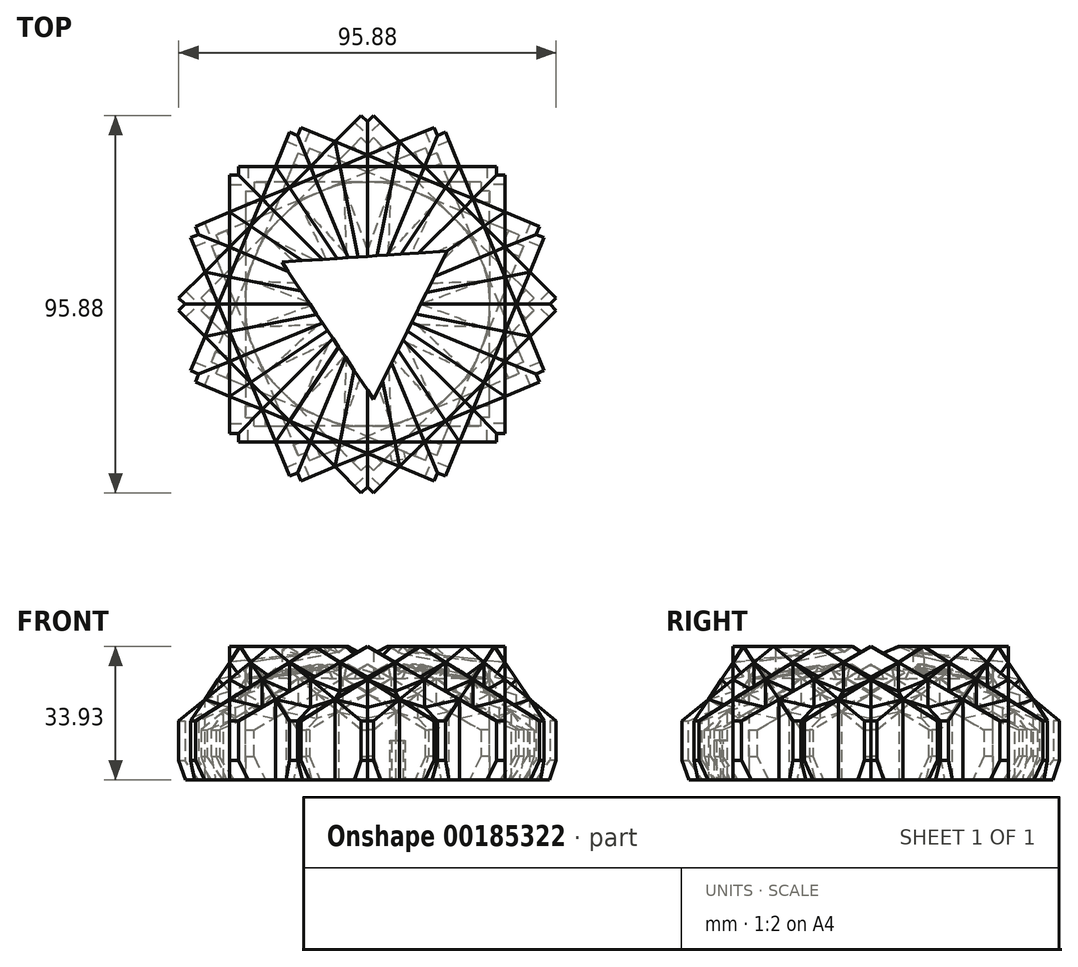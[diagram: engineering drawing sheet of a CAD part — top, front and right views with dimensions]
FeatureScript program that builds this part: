
annotation { "Feature Type Name" : "Feature", "Feature Type Description" : "" }
export const myFeature = defineFeature(function(context is Context, id is Id, definition is map)
    precondition{}
    {
        {
            var Q0;
            Q0=qCreatedBy(makeId("Front.planeOp"),FACE);
            var sketch = newSketch(context, id + "F0", { "sketchPlane" : qUnion([Q0])});
            skLineSegment(sketch, "E0", {"start": v(4.08, -77.3) * mm, "end": v(4.08, 73.55) * mm, "construction": true});
            skCircle(sketch, "E1.cCircle", {"center": v(4.08, -2.77) * mm, "radius": 37.87 * mm, "construction": true});
            skLineSegment(sketch, "E1.0", {"start": v(4.08, 35.1) * mm, "end": v(36.87, -21.7) * mm});
            skLineSegment(sketch, "E1.1", {"start": v(36.87, -21.7) * mm, "end": v(-28.71, -21.7) * mm});
            skLineSegment(sketch, "E1.2", {"start": v(-28.71, -21.7) * mm, "end": v(4.08, 35.1) * mm});
            skLineSegment(sketch, "E2.0", {"start": v(4.08, 35.1) * mm, "end": v(36.87, 16.17) * mm});
            skLineSegment(sketch, "E2.1", {"start": v(36.87, 16.17) * mm, "end": v(36.87, -21.7) * mm});
            skLineSegment(sketch, "E2.2", {"start": v(36.87, -21.7) * mm, "end": v(4.08, -40.63) * mm});
            skLineSegment(sketch, "E2.3", {"start": v(4.08, -40.63) * mm, "end": v(-28.71, -21.7) * mm});
            skLineSegment(sketch, "E2.4", {"start": v(-28.71, -21.7) * mm, "end": v(-28.71, 16.17) * mm});
            skLineSegment(sketch, "E2.5", {"start": v(-28.71, 16.17) * mm, "end": v(4.08, 35.1) * mm});
            skLineSegment(sketch, "E3", {"start": v(4.08, -15.7) * mm, "end": v(4.08, -21.7) * mm, "construction": true});
            skLineSegment(sketch, "E4", {"start": v(-28.71, -21.7) * mm, "end": v(-21.71, -21.7) * mm, "construction": true});
            skArc(sketch, "E5", {"start": v(4.08, -15.7) * mm, "mid": v(-9.22, -16.96) * mm, "end": v(-21.71, -21.7) * mm});
            skArc(sketch, "E6.MirrorCS", {"start": v(4.08, -15.7) * mm, "mid": v(17.38, -16.96) * mm, "end": v(29.87, -21.7) * mm});
            skArc(sketch, "E7", {"start": v(-12.32, 25.63) * mm, "mid": v(4.08, 3.7) * mm, "end": v(20.48, 25.63) * mm});
            skLineSegment(sketch, "E8", {"start": v(-12.32, 25.63) * mm, "end": v(-20.53, 16.17) * mm});
            skLineSegment(sketch, "E9", {"start": v(-20.53, 16.17) * mm, "end": v(-28.71, 16.17) * mm});
            skLineSegment(sketch, "E10.MirrorCS", {"start": v(20.48, 25.63) * mm, "end": v(28.7, 16.17) * mm});
            skLineSegment(sketch, "E11.MirrorCS", {"start": v(28.7, 16.17) * mm, "end": v(36.87, 16.17) * mm});
            skLineSegment(sketch, "E12", {"start": v(-28.71, 16.17) * mm, "end": v(-28.71, 6.17) * mm, "construction": true});
            skLineSegment(sketch, "E13", {"start": v(-28.71, 6.17) * mm, "end": v(-28.71, -3.83) * mm, "construction": true});
            skArc(sketch, "E14", {"start": v(-28.71, -3.83) * mm, "mid": v(-26.27, 1.17) * mm, "end": v(-28.71, 6.17) * mm});
            skArc(sketch, "E15.MirrorCS", {"start": v(36.87, -3.83) * mm, "mid": v(34.42, 1.17) * mm, "end": v(36.87, 6.17) * mm});
            skLineSegment(sketch, "E16", {"start": v(-28.71, 1.17) * mm, "end": v(-26.27, 1.17) * mm, "construction": true});
            skLineSegment(sketch, "E17", {"start": v(-28.71, 6.17) * mm, "end": v(-26.27, 1.17) * mm});
            skLineSegment(sketch, "E18", {"start": v(-26.27, 1.17) * mm, "end": v(-28.71, -3.83) * mm});
            skLineSegment(sketch, "E19.MirrorCS", {"start": v(36.87, 6.17) * mm, "end": v(34.42, 1.17) * mm});
            skLineSegment(sketch, "E20.MirrorCS", {"start": v(34.42, 1.17) * mm, "end": v(36.87, -3.83) * mm});
            skLineSegment(sketch, "E21", {"start": v(-28.71, 1.17) * mm, "end": v(36.87, 1.17) * mm});
            skSolve(sketch);
        }
        {
            var Q0;
            {var subQ0=sQuery(id+"F0.wireOp",EDGE,"E8");Q0=makeQuery(id+"F0.imprint","IMPRINT",FACE,{"disambiguationData":[TD([[makeQuery(id+"F0.imprint","IMPRINT",EDGE,{"derivedFrom":subQ0}),1.0]])]});}
            var Q1;
            {var subQ0=sQuery(id+"F0.wireOp",EDGE,"E7");var subQ1=sQuery(id+"F0.wireOp",EDGE,"E1.0");var subQ2=makeQuery(id+"F0.imprint","INTERSECT",VERTEX,{"derivedFrom":[subQ1,subQ0]});Q1=makeQuery(id+"F0.imprint","IMPRINT",FACE,{"disambiguationData":[TD([[makeQuery(id+"F0.imprint","IMPRINT",EDGE,{"disambiguationData":[TD([[subQ2,-1.0]])],"derivedFrom":subQ1}),-1.0]])]});}
            var Q2;
            {var subQ0=sQuery(id+"F0.wireOp",EDGE,"E10.MirrorCS");Q2=makeQuery(id+"F0.imprint","IMPRINT",FACE,{"disambiguationData":[TD([[makeQuery(id+"F0.imprint","IMPRINT",EDGE,{"derivedFrom":subQ0}),-1.0]])]});}
            var Q3;
            {var subQ2=sQuery(id+"F0.wireOp",EDGE,"E10.MirrorCS");Q3=makeQuery(id+"F0.imprint","IMPRINT",FACE,{"disambiguationData":[TD([[makeQuery(id+"F0.imprint","IMPRINT",EDGE,{"derivedFrom":subQ2}),1.0]])]});}
            var Q4;
            {var subQ1=sQuery(id+"F0.wireOp",EDGE,"E1.0");var subQ3=sQuery(id+"F0.wireOp",EDGE,"E7");var subQ4=makeQuery(id+"F0.imprint","INTERSECT",VERTEX,{"derivedFrom":[subQ1,subQ3]});Q4=makeQuery(id+"F0.imprint","IMPRINT",FACE,{"disambiguationData":[TD([[makeQuery(id+"F0.imprint","IMPRINT",EDGE,{"disambiguationData":[TD([[subQ4,-1.0]])],"derivedFrom":subQ3}),1.0]])]});}
            var Q5;
            {var subQ1=sQuery(id+"F0.wireOp",EDGE,"E1.2");var subQ3=sQuery(id+"F0.wireOp",EDGE,"E7");var subQ4=makeQuery(id+"F0.imprint","INTERSECT",VERTEX,{"derivedFrom":[subQ1,subQ3]});Q5=makeQuery(id+"F0.imprint","IMPRINT",FACE,{"disambiguationData":[TD([[makeQuery(id+"F0.imprint","IMPRINT",EDGE,{"disambiguationData":[TD([[subQ4,1.0]])],"derivedFrom":subQ3}),1.0]])]});}
            var Q6;
            {var subQ0=sQuery(id+"F0.wireOp",EDGE,"E17");Q6=makeQuery(id+"F0.imprint","IMPRINT",FACE,{"disambiguationData":[TD([[makeQuery(id+"F0.imprint","IMPRINT",EDGE,{"derivedFrom":subQ0}),1.0]])]});}
            var Q7;
            {var subQ0=sQuery(id+"F0.wireOp",EDGE,"E19.MirrorCS");Q7=makeQuery(id+"F0.imprint","IMPRINT",FACE,{"disambiguationData":[TD([[makeQuery(id+"F0.imprint","IMPRINT",EDGE,{"derivedFrom":subQ0}),-1.0]])]});}
            var Q8;
            {var subQ1=sQuery(id+"F0.wireOp",EDGE,"E1.0");var subQ3=sQuery(id+"F0.wireOp",EDGE,"E7");var subQ4=makeQuery(id+"F0.imprint","INTERSECT",VERTEX,{"derivedFrom":[subQ1,subQ3]});Q8=makeQuery(id+"F0.imprint","IMPRINT",FACE,{"disambiguationData":[TD([[makeQuery(id+"F0.imprint","IMPRINT",EDGE,{"disambiguationData":[TD([[subQ4,1.0]])],"derivedFrom":subQ3}),1.0]])]});}
            var Q9;
            {var subQ2=sQuery(id+"F0.wireOp",EDGE,"E8");Q9=makeQuery(id+"F0.imprint","IMPRINT",FACE,{"disambiguationData":[TD([[makeQuery(id+"F0.imprint","IMPRINT",EDGE,{"derivedFrom":subQ2}),-1.0]])]});}
            var Q10;
            {var subQ1=sQuery(id+"F0.wireOp",EDGE,"E1.0");var subQ3=sQuery(id+"F0.wireOp",EDGE,"6VoTTzTf-1nzT-aMky-r3Jn-bNhaZYPHa5TC");var subQ4=makeQuery(id+"F0.imprint","INTERSECT",VERTEX,{"derivedFrom":[subQ1,subQ3]});Q10=makeQuery(id+"F0.imprint","IMPRINT",FACE,{"disambiguationData":[TD([[makeQuery(id+"F0.imprint","IMPRINT",EDGE,{"disambiguationData":[TD([[subQ4,-1.0]])],"derivedFrom":subQ3}),-1.0]])]});}
            var Q11;
            Q11=sQuery(id+"F0.wireOp",EDGE,"E1.0");
            var Q12;
            Q12=sQuery(id+"F0.wireOp",EDGE,"E1.1");
            var Q13;
            Q13=sQuery(id+"F0.wireOp",EDGE,"E1.2");
            var Q14;
            Q14=sQuery(id+"F0.wireOp",EDGE,"E2.0");
            var Q15;
            Q15=sQuery(id+"F0.wireOp",EDGE,"E2.1");
            var Q16;
            Q16=sQuery(id+"F0.wireOp",EDGE,"E2.2");
            var Q17;
            Q17=sQuery(id+"F0.wireOp",EDGE,"E2.3");
            var Q18;
            Q18=sQuery(id+"F0.wireOp",EDGE,"E2.4");
            var Q19;
            Q19=sQuery(id+"F0.wireOp",EDGE,"E2.5");
            var Q20;
            Q20=sQuery(id+"F0.wireOp",EDGE,"E5");
            var Q21;
            Q21=sQuery(id+"F0.wireOp",EDGE,"E6.MirrorCS");
            var Q22;
            Q22=sQuery(id+"F0.wireOp",EDGE,"E7");
            var Q23;
            Q23=sQuery(id+"F0.wireOp",EDGE,"E8");
            var Q24;
            Q24=sQuery(id+"F0.wireOp",EDGE,"E9");
            var Q25;
            Q25=sQuery(id+"F0.wireOp",EDGE,"E10.MirrorCS");
            var Q26;
            Q26=sQuery(id+"F0.wireOp",EDGE,"E11.MirrorCS");
            var Q27;
            Q27=sQuery(id+"F0.wireOp",EDGE,"E14");
            var Q28;
            Q28=sQuery(id+"F0.wireOp",EDGE,"E15.MirrorCS");
            var Q29;
            Q29=sQuery(id+"F0.wireOp",EDGE,"E17");
            var Q30;
            Q30=sQuery(id+"F0.wireOp",EDGE,"E18");
            var Q31;
            Q31=sQuery(id+"F0.wireOp",EDGE,"E19.MirrorCS");
            var Q32;
            Q32=sQuery(id+"F0.wireOp",EDGE,"E20.MirrorCS");
            var Q33;
            Q33=sQuery(id+"F0.wireOp",EDGE,"E21");
            extrude(context, id + "F1", {"entities" : qUnion([Q0, Q1, Q2, Q3, Q4, Q5, Q6, Q7, Q8, Q9, Q10]), "surfaceEntities" : qUnion([Q11, Q12, Q13, Q14, Q15, Q16, Q17, Q18, Q19, Q20, Q21, Q22, Q23, Q24, Q25, Q26, Q27, Q28, Q29, Q30, Q31, Q32, Q33]), "offsetDistance" : 25 * mm, "depth" : 35 * mm});
        }
        {
            var Q0;
            Q0=makeQuery(id+"F1.opExtrude","SWEPT_BODY",BODY,{"disambiguationData":[OSD([sQuery(id+"F0.wireOp",EDGE,"E2.0"),sQuery(id+"F0.wireOp",EDGE,"E2.1"),sQuery(id+"F0.wireOp",EDGE,"E2.4"),sQuery(id+"F0.wireOp",EDGE,"E2.5"),sQuery(id+"F0.wireOp",EDGE,"E17"),sQuery(id+"F0.wireOp",EDGE,"E19.MirrorCS"),sQuery(id+"F0.wireOp",EDGE,"E21")])]});
            var Q1;
            Q1=sQuery(id+"F0.wireOp",EDGE,"E0");
            circularPattern(context, id + "F2", {"operationType" : NewBodyOperationType.ADD, "entities" : qUnion([Q0]), "axis" : qUnion([Q1]), "angle" : 360 * degree, "instanceCount" : 16, "equalSpace" : true, "isCentered" : true});
        }
        {
            var Q0;
            {var subQ0=makeQuery(id+"F1.opExtrude","SWEPT_FACE",FACE,{"disambiguationData":[OSD([sQuery(id+"F0.wireOp",EDGE,"E21")])]});Q0=makeQuery(id+"F2.boolean.opBoolean","MERGE",FACE,{"derivedFrom":[subQ0,makeQuery(id+"F2.opPattern","COPY",FACE,{"derivedFrom":subQ0,"instanceName":"-15"}),makeQuery(id+"F2.opPattern","COPY",FACE,{"derivedFrom":subQ0,"instanceName":"-14"}),makeQuery(id+"F2.opPattern","COPY",FACE,{"derivedFrom":subQ0,"instanceName":"-13"}),makeQuery(id+"F2.opPattern","COPY",FACE,{"derivedFrom":subQ0,"instanceName":"-12"}),makeQuery(id+"F2.opPattern","COPY",FACE,{"derivedFrom":subQ0,"instanceName":"-11"}),makeQuery(id+"F2.opPattern","COPY",FACE,{"derivedFrom":subQ0,"instanceName":"-10"}),makeQuery(id+"F2.opPattern","COPY",FACE,{"derivedFrom":subQ0,"instanceName":"-9"}),makeQuery(id+"F2.opPattern","COPY",FACE,{"derivedFrom":subQ0,"instanceName":"-8"}),makeQuery(id+"F2.opPattern","COPY",FACE,{"derivedFrom":subQ0,"instanceName":"-7"}),makeQuery(id+"F2.opPattern","COPY",FACE,{"derivedFrom":subQ0,"instanceName":"-6"}),makeQuery(id+"F2.opPattern","COPY",FACE,{"derivedFrom":subQ0,"instanceName":"-5"}),makeQuery(id+"F2.opPattern","COPY",FACE,{"derivedFrom":subQ0,"instanceName":"-4"}),makeQuery(id+"F2.opPattern","COPY",FACE,{"derivedFrom":subQ0,"instanceName":"-3"}),makeQuery(id+"F2.opPattern","COPY",FACE,{"derivedFrom":subQ0,"instanceName":"-2"}),makeQuery(id+"F2.opPattern","COPY",FACE,{"derivedFrom":subQ0,"instanceName":"-1"}),makeQuery(id+"F2.opPattern","COPY",FACE,{"derivedFrom":subQ0,"instanceName":"1"}),makeQuery(id+"F2.opPattern","COPY",FACE,{"derivedFrom":subQ0,"instanceName":"2"}),makeQuery(id+"F2.opPattern","COPY",FACE,{"derivedFrom":subQ0,"instanceName":"3"}),makeQuery(id+"F2.opPattern","COPY",FACE,{"derivedFrom":subQ0,"instanceName":"4"}),makeQuery(id+"F2.opPattern","COPY",FACE,{"derivedFrom":subQ0,"instanceName":"5"}),makeQuery(id+"F2.opPattern","COPY",FACE,{"derivedFrom":subQ0,"instanceName":"6"}),makeQuery(id+"F2.opPattern","COPY",FACE,{"derivedFrom":subQ0,"instanceName":"7"}),makeQuery(id+"F2.opPattern","COPY",FACE,{"derivedFrom":subQ0,"instanceName":"8"}),makeQuery(id+"F2.opPattern","COPY",FACE,{"derivedFrom":subQ0,"instanceName":"9"}),makeQuery(id+"F2.opPattern","COPY",FACE,{"derivedFrom":subQ0,"instanceName":"10"}),makeQuery(id+"F2.opPattern","COPY",FACE,{"derivedFrom":subQ0,"instanceName":"11"}),makeQuery(id+"F2.opPattern","COPY",FACE,{"derivedFrom":subQ0,"instanceName":"12"}),makeQuery(id+"F2.opPattern","COPY",FACE,{"derivedFrom":subQ0,"instanceName":"13"}),makeQuery(id+"F2.opPattern","COPY",FACE,{"derivedFrom":subQ0,"instanceName":"14"}),makeQuery(id+"F2.opPattern","COPY",FACE,{"derivedFrom":subQ0,"instanceName":"15"})]});}
            shell(context, id + "F3", {"entities" : qUnion([Q0]), "thickness" : 4 * mm});
        }
        {
            var Q0;
            {var subQ0=makeQuery(id+"F1.opExtrude","SWEPT_FACE",FACE,{"disambiguationData":[OSD([sQuery(id+"F0.wireOp",EDGE,"E21")])]});Q0=makeQuery(id+"F2.boolean.opBoolean","MERGE",FACE,{"derivedFrom":[subQ0,makeQuery(id+"F2.opPattern","COPY",FACE,{"derivedFrom":subQ0,"instanceName":"-15"}),makeQuery(id+"F2.opPattern","COPY",FACE,{"derivedFrom":subQ0,"instanceName":"-14"}),makeQuery(id+"F2.opPattern","COPY",FACE,{"derivedFrom":subQ0,"instanceName":"-13"}),makeQuery(id+"F2.opPattern","COPY",FACE,{"derivedFrom":subQ0,"instanceName":"-12"}),makeQuery(id+"F2.opPattern","COPY",FACE,{"derivedFrom":subQ0,"instanceName":"-11"}),makeQuery(id+"F2.opPattern","COPY",FACE,{"derivedFrom":subQ0,"instanceName":"-10"}),makeQuery(id+"F2.opPattern","COPY",FACE,{"derivedFrom":subQ0,"instanceName":"-9"}),makeQuery(id+"F2.opPattern","COPY",FACE,{"derivedFrom":subQ0,"instanceName":"-8"}),makeQuery(id+"F2.opPattern","COPY",FACE,{"derivedFrom":subQ0,"instanceName":"-7"}),makeQuery(id+"F2.opPattern","COPY",FACE,{"derivedFrom":subQ0,"instanceName":"-6"}),makeQuery(id+"F2.opPattern","COPY",FACE,{"derivedFrom":subQ0,"instanceName":"-5"}),makeQuery(id+"F2.opPattern","COPY",FACE,{"derivedFrom":subQ0,"instanceName":"-4"}),makeQuery(id+"F2.opPattern","COPY",FACE,{"derivedFrom":subQ0,"instanceName":"-3"}),makeQuery(id+"F2.opPattern","COPY",FACE,{"derivedFrom":subQ0,"instanceName":"-2"}),makeQuery(id+"F2.opPattern","COPY",FACE,{"derivedFrom":subQ0,"instanceName":"-1"}),makeQuery(id+"F2.opPattern","COPY",FACE,{"derivedFrom":subQ0,"instanceName":"1"}),makeQuery(id+"F2.opPattern","COPY",FACE,{"derivedFrom":subQ0,"instanceName":"2"}),makeQuery(id+"F2.opPattern","COPY",FACE,{"derivedFrom":subQ0,"instanceName":"3"}),makeQuery(id+"F2.opPattern","COPY",FACE,{"derivedFrom":subQ0,"instanceName":"4"}),makeQuery(id+"F2.opPattern","COPY",FACE,{"derivedFrom":subQ0,"instanceName":"5"}),makeQuery(id+"F2.opPattern","COPY",FACE,{"derivedFrom":subQ0,"instanceName":"6"}),makeQuery(id+"F2.opPattern","COPY",FACE,{"derivedFrom":subQ0,"instanceName":"7"}),makeQuery(id+"F2.opPattern","COPY",FACE,{"derivedFrom":subQ0,"instanceName":"8"}),makeQuery(id+"F2.opPattern","COPY",FACE,{"derivedFrom":subQ0,"instanceName":"9"}),makeQuery(id+"F2.opPattern","COPY",FACE,{"derivedFrom":subQ0,"instanceName":"10"}),makeQuery(id+"F2.opPattern","COPY",FACE,{"derivedFrom":subQ0,"instanceName":"11"}),makeQuery(id+"F2.opPattern","COPY",FACE,{"derivedFrom":subQ0,"instanceName":"12"}),makeQuery(id+"F2.opPattern","COPY",FACE,{"derivedFrom":subQ0,"instanceName":"13"}),makeQuery(id+"F2.opPattern","COPY",FACE,{"derivedFrom":subQ0,"instanceName":"14"}),makeQuery(id+"F2.opPattern","COPY",FACE,{"derivedFrom":subQ0,"instanceName":"15"})]});}
            var sketch = newSketch(context, id + "F4", { "sketchPlane" : qUnion([Q0])});
            skLineSegment(sketch, "E22.bottom", {"start": v(9.25, 34.95) * mm, "end": v(12.68, 34.26) * mm});
            skLineSegment(sketch, "E22.top", {"start": v(10.22, 39.85) * mm, "end": v(13.65, 39.17) * mm});
            skLineSegment(sketch, "E22.left", {"start": v(9.25, 34.95) * mm, "end": v(10.22, 39.85) * mm});
            skLineSegment(sketch, "E22.right", {"start": v(12.68, 34.26) * mm, "end": v(13.65, 39.17) * mm});
            skPoint(sketch, "E22.middle", {"position": v(11.45, 37.06) * mm});
            skLineSegment(sketch, "E23", {"start": v(11.35, 36.57) * mm, "end": v(11.94, 39.5) * mm, "construction": true});
            skLineSegment(sketch, "E24", {"start": v(11.45, 37.06) * mm, "end": v(13.17, 36.72) * mm, "construction": true});
            skLineSegment(sketch, "E25", {"start": v(11.45, 37.06) * mm, "end": v(9.73, 37.4) * mm, "construction": true});
            skLineSegment(sketch, "E26", {"start": v(12.3, 41.29) * mm, "end": v(11.35, 36.57) * mm, "construction": true});
            skSolve(sketch);
        }
        {
            var Q0;
            Q0 = qSketchRegion(id + "F4", true);
            extrude(context, id + "F5", {"entities" : qUnion([Q0]), "operationType" : NewBodyOperationType.REMOVE, "oppositeDirection" : true, "depth" : 10 * mm, "offsetDistance" : 25 * mm});
        }
        {
            var Q0;
            Q0=qCreatedBy(makeId("Front.planeOp"),FACE);
            var sketch = newSketch(context, id + "F6", { "sketchPlane" : qUnion([Q0])});
            skLineSegment(sketch, "E27.0", {"start": v(35.25, 26.89) * mm, "end": v(35.08, 30.48) * mm});
            skLineSegment(sketch, "E27.1", {"start": v(35.08, 30.48) * mm, "end": v(17.6, 30.48) * mm});
            skLineSegment(sketch, "E28", {"start": v(17.6, 30.48) * mm, "end": v(35.25, 26.89) * mm});
            skSolve(sketch);
        }
        {
            var Q0;
            Q0=makeQuery(id+"F6.imprint","IMPRINT",FACE,{"disambiguationData":[TD([[makeQuery(id+"F6.imprint","IMPRINT",EDGE,{"derivedFrom":sQuery(id+"F6.wireOp",EDGE,"E27.0")}),1.0]])]});
            var Q1;
            Q1=sQuery(id+"F0.wireOp",EDGE,"E0");
            revolve(context, id + "F7", {"operationType" : NewBodyOperationType.ADD, "surfaceOperationType" : NewSurfaceOperationType.NEW, "entities" : qUnion([Q0]), "axis" : qUnion([Q1]), "revolveType" : RevolveType.FULL});
        }
        {
            var Q0;
            Q0=qCreatedBy(makeId("Top.planeOp"),FACE);
            var sketch = newSketch(context, id + "F8", { "sketchPlane" : qUnion([Q0])});
            skCircle(sketch, "E29.cCircle", {"center": v(4.08, 0) * mm, "radius": 12.12 * mm, "construction": true});
            skLineSegment(sketch, "E29.0", {"start": v(24.24, 13.47) * mm, "end": v(5.66, -24.2) * mm});
            skLineSegment(sketch, "E29.1", {"start": v(5.66, -24.2) * mm, "end": v(-17.67, 10.72) * mm});
            skLineSegment(sketch, "E29.2", {"start": v(-17.67, 10.72) * mm, "end": v(24.24, 13.47) * mm});
            skPoint(sketch, "E29.0.midPoint", {"position": v(14.95, -5.36) * mm});
            skLineSegment(sketch, "E30", {"start": v(4.08, 0) * mm, "end": v(3.29, 12.1) * mm, "construction": true});
            skLineSegment(sketch, "E31.0", {"start": v(4.08, 0) * mm, "end": v(33.75, 19.83) * mm});
            skSolve(sketch);
        }
        {
            var Q0;
            Q0 = qSketchRegion(id + "F8", true);
            extrude(context, id + "F9", {"entities" : qUnion([Q0]), "operationType" : NewBodyOperationType.REMOVE, "endBound" : BoundingType.THROUGH_ALL, "depth" : 25 * mm, "offsetDistance" : 25 * mm});
        }
    });
